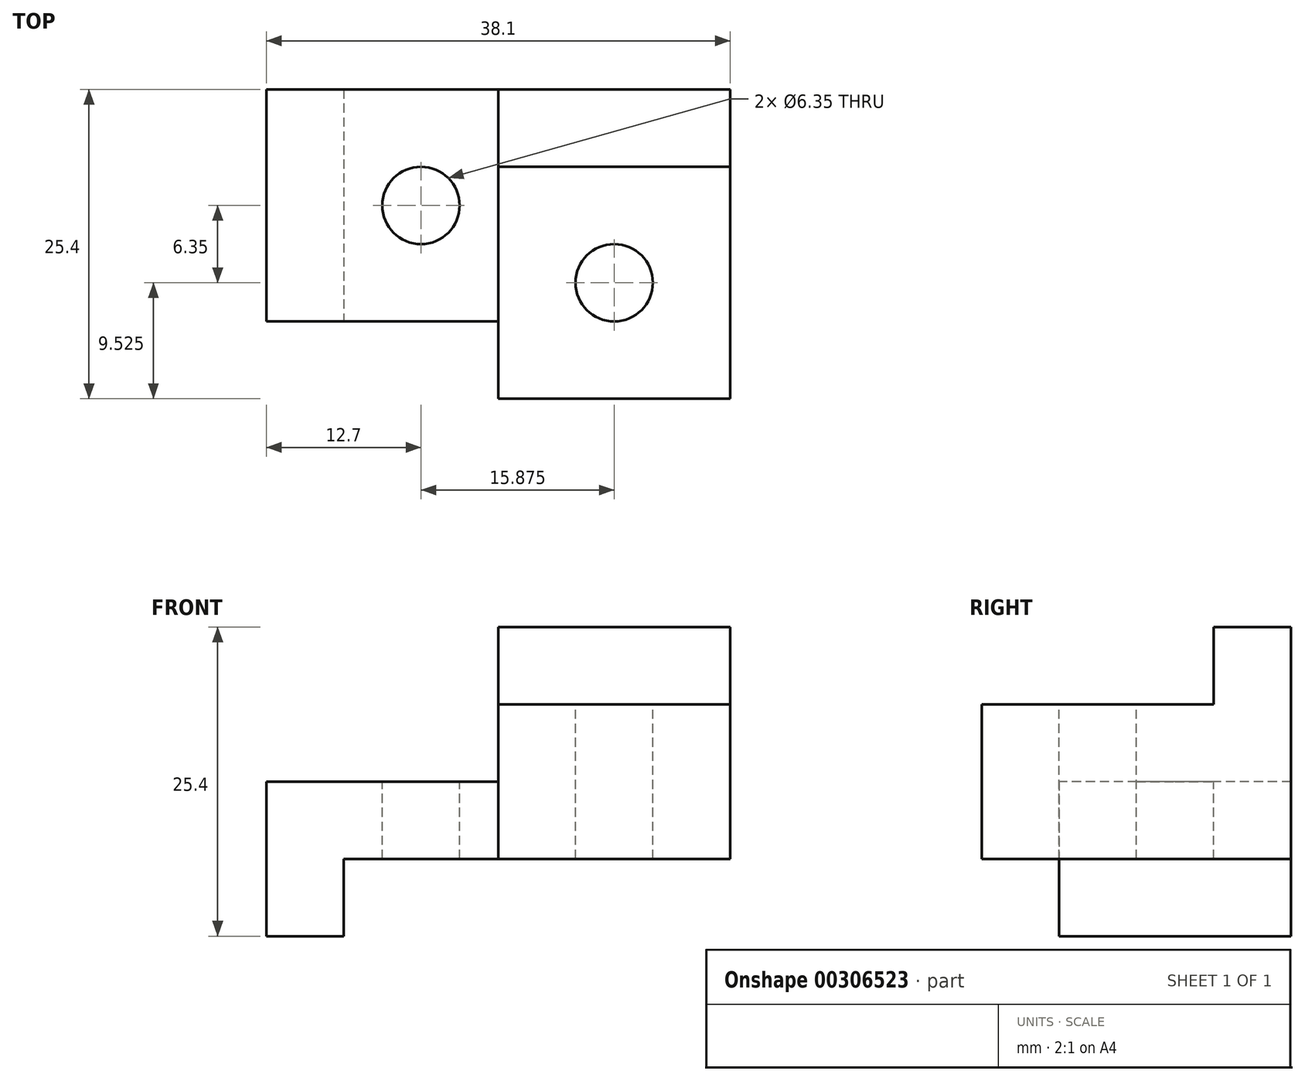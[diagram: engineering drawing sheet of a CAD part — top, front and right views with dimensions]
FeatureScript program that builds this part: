
annotation { "Feature Type Name" : "Feature", "Feature Type Description" : "" }
export const myFeature = defineFeature(function(context is Context, id is Id, definition is map)
    precondition{}
    {
        {
            var Q0;
            Q0=qCreatedBy(makeId("Top.planeOp"),FACE);
            var sketch = newSketch(context, id + "F0", { "sketchPlane" : qUnion([Q0])});
            skLineSegment(sketch, "E0", {"start": v(0, 0) * mm, "end": v(0, 19.05) * mm});
            skLineSegment(sketch, "E1", {"start": v(0, 19.05) * mm, "end": v(38.1, 19.05) * mm});
            skLineSegment(sketch, "E2", {"start": v(38.1, 19.05) * mm, "end": v(38.1, -6.35) * mm});
            skLineSegment(sketch, "E3", {"start": v(38.1, -6.35) * mm, "end": v(19.05, -6.35) * mm});
            skLineSegment(sketch, "E4", {"start": v(19.05, -6.35) * mm, "end": v(19.05, 0) * mm});
            skLineSegment(sketch, "E5", {"start": v(19.05, 0) * mm, "end": v(0, 0) * mm});
            skSolve(sketch);
        }
        {
            var Q0;
            Q0 = qSketchRegion(id + "F0", true);
            extrude(context, id + "F1", {"entities" : qUnion([Q0]), "depth" : 19.05 * mm});
        }
        {
            var Q0;
            Q0=makeQuery(id+"F1.opExtrude","SWEPT_FACE",FACE,{"disambiguationData":[OSD([sQuery(id+"F0.wireOp",EDGE,"E5")])]});
            var sketch = newSketch(context, id + "F2", { "sketchPlane" : qUnion([Q0])});
            skLineSegment(sketch, "E6.bottom", {"start": v(0, 19.05) * mm, "end": v(19.05, 19.05) * mm});
            skLineSegment(sketch, "E6.top", {"start": v(0, 6.35) * mm, "end": v(19.05, 6.35) * mm});
            skLineSegment(sketch, "E6.left", {"start": v(0, 19.05) * mm, "end": v(0, 6.35) * mm});
            skLineSegment(sketch, "E6.right", {"start": v(19.05, 19.05) * mm, "end": v(19.05, 6.35) * mm});
            skSolve(sketch);
        }
        {
            var Q0;
            Q0 = qSketchRegion(id + "F2", true);
            extrude(context, id + "F3", {"entities" : qUnion([Q0]), "operationType" : NewBodyOperationType.REMOVE, "endBound" : BoundingType.THROUGH_ALL, "oppositeDirection" : true, "depth" : 25.4 * mm});
        }
        {
            var Q0;
            Q0=makeQuery(id+"F1.opExtrude","SWEPT_FACE",FACE,{"disambiguationData":[OSD([sQuery(id+"F0.wireOp",EDGE,"E3")])]});
            var sketch = newSketch(context, id + "F4", { "sketchPlane" : qUnion([Q0])});
            skLineSegment(sketch, "E7.bottom", {"start": v(19.05, 19.05) * mm, "end": v(38.1, 19.05) * mm});
            skLineSegment(sketch, "E7.top", {"start": v(19.05, 12.7) * mm, "end": v(38.1, 12.7) * mm});
            skLineSegment(sketch, "E7.left", {"start": v(19.05, 19.05) * mm, "end": v(19.05, 12.7) * mm});
            skLineSegment(sketch, "E7.right", {"start": v(38.1, 19.05) * mm, "end": v(38.1, 12.7) * mm});
            skSolve(sketch);
        }
        {
            var Q0;
            Q0 = qSketchRegion(id + "F4", true);
            extrude(context, id + "F5", {"entities" : qUnion([Q0]), "operationType" : NewBodyOperationType.REMOVE, "oppositeDirection" : true, "depth" : 19.05 * mm});
        }
        {
            var Q0;
            Q0=qCreatedBy(makeId("Front.planeOp"),FACE);
            var sketch = newSketch(context, id + "F6", { "sketchPlane" : qUnion([Q0])});
            skLineSegment(sketch, "E8.bottom", {"start": v(0, 0) * mm, "end": v(6.35, 0) * mm});
            skLineSegment(sketch, "E8.top", {"start": v(0, -6.35) * mm, "end": v(6.35, -6.35) * mm});
            skLineSegment(sketch, "E8.left", {"start": v(0, 0) * mm, "end": v(0, -6.35) * mm});
            skLineSegment(sketch, "E8.right", {"start": v(6.35, 0) * mm, "end": v(6.35, -6.35) * mm});
            skSolve(sketch);
        }
        {
            var Q0;
            Q0 = qSketchRegion(id + "F6", true);
            extrude(context, id + "F7", {"entities" : qUnion([Q0]), "operationType" : NewBodyOperationType.ADD, "oppositeDirection" : true, "depth" : 19.05 * mm});
        }
        {
            var Q0;
            Q0=makeQuery(id+"F3.boolean.opBoolean","COPY",FACE,{"derivedFrom":makeQuery(id+"F3.opExtrude","SWEPT_FACE",FACE,{"disambiguationData":[OSD([sQuery(id+"F2.wireOp",EDGE,"E6.top")])]})});
            var sketch = newSketch(context, id + "F8", { "sketchPlane" : qUnion([Q0])});
            skCircle(sketch, "E9", {"center": v(12.7, 9.53) * mm, "radius": 3.18 * mm});
            skLineSegment(sketch, "E10", {"start": v(0, 9.53) * mm, "end": v(54.72, 9.53) * mm, "construction": true});
            skSolve(sketch);
        }
        {
            var Q0;
            Q0 = qSketchRegion(id + "F8", true);
            extrude(context, id + "F9", {"entities" : qUnion([Q0]), "operationType" : NewBodyOperationType.REMOVE, "endBound" : BoundingType.THROUGH_ALL, "oppositeDirection" : true, "depth" : 25.4 * mm});
        }
        {
            var Q0;
            Q0=makeQuery(id+"F5.boolean.opBoolean","COPY",FACE,{"derivedFrom":makeQuery(id+"F5.opExtrude","SWEPT_FACE",FACE,{"disambiguationData":[OSD([sQuery(id+"F4.wireOp",EDGE,"E7.top")])]})});
            var sketch = newSketch(context, id + "F10", { "sketchPlane" : qUnion([Q0])});
            skCircle(sketch, "E11", {"center": v(28.57, 3.18) * mm, "radius": 3.18 * mm});
            skPoint(sketch, "E11.centerSnap0", {"position": v(28.57, -6.35) * mm});
            skLineSegment(sketch, "E12", {"start": v(28.57, -6.35) * mm, "end": v(28.57, 26.74) * mm, "construction": true});
            skPoint(sketch, "E12.endSnap0", {"position": v(28.57, 12.7) * mm});
            skLineSegment(sketch, "E13", {"start": v(19.05, 3.18) * mm, "end": v(48.91, 3.18) * mm, "construction": true});
            skSolve(sketch);
        }
        {
            var Q0;
            Q0 = qSketchRegion(id + "F10", true);
            extrude(context, id + "F11", {"entities" : qUnion([Q0]), "operationType" : NewBodyOperationType.REMOVE, "endBound" : BoundingType.THROUGH_ALL, "oppositeDirection" : true, "depth" : 25.4 * mm});
        }
    });
